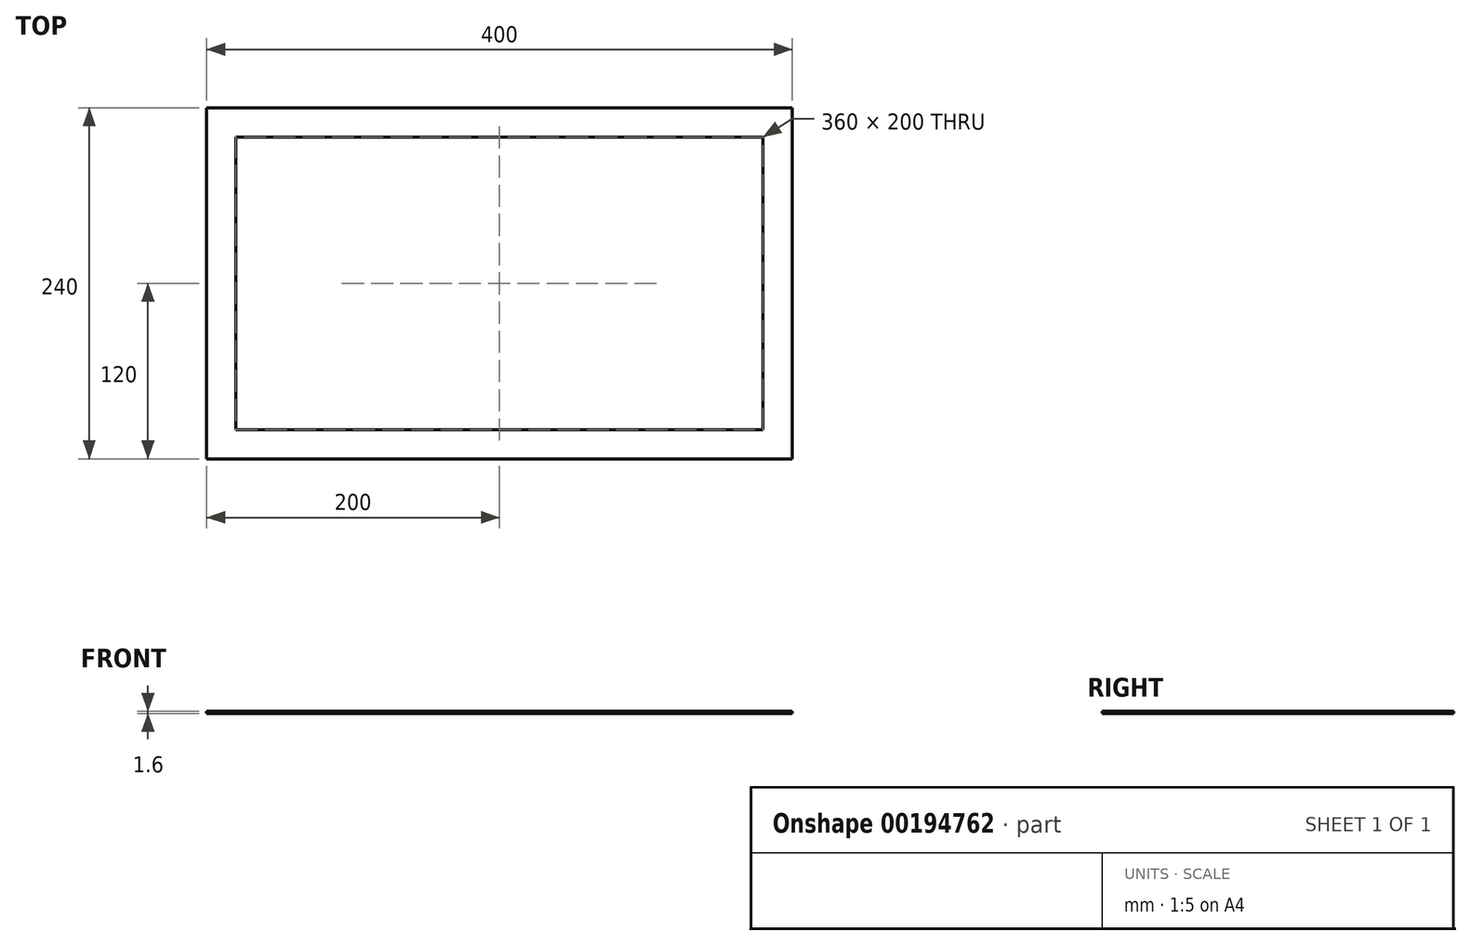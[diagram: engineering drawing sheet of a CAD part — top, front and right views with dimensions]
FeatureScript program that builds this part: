
annotation { "Feature Type Name" : "Feature", "Feature Type Description" : "" }
export const myFeature = defineFeature(function(context is Context, id is Id, definition is map)
    precondition{}
    {
        {
            var Q0;
            Q0=qCreatedBy(makeId("Top.planeOp"),FACE);
            var sketch = newSketch(context, id + "F0", { "sketchPlane" : qUnion([Q0])});
            skLineSegment(sketch, "E0.bottom", {"start": v(200, 120) * mm, "end": v(-200, 120) * mm});
            skLineSegment(sketch, "E0.top", {"start": v(200, -120) * mm, "end": v(-200, -120) * mm});
            skLineSegment(sketch, "E0.left", {"start": v(200, 120) * mm, "end": v(200, -120) * mm});
            skLineSegment(sketch, "E0.right", {"start": v(-200, 120) * mm, "end": v(-200, -120) * mm});
            skPoint(sketch, "E0.middle", {"position": v(0, 0) * mm});
            skLineSegment(sketch, "E1.bottom", {"start": v(180, 100) * mm, "end": v(-180, 100) * mm});
            skLineSegment(sketch, "E1.top", {"start": v(180, -100) * mm, "end": v(-180, -100) * mm});
            skLineSegment(sketch, "E1.left", {"start": v(180, 100) * mm, "end": v(180, -100) * mm});
            skLineSegment(sketch, "E1.right", {"start": v(-180, 100) * mm, "end": v(-180, -100) * mm});
            skSolve(sketch);
        }
        {
            var Q0;
            Q0 = qSketchRegion(id + "F0", true);
            extrude(context, id + "F1", {"entities" : qUnion([Q0]), "depth" : 1.6 * mm});
        }
    });
